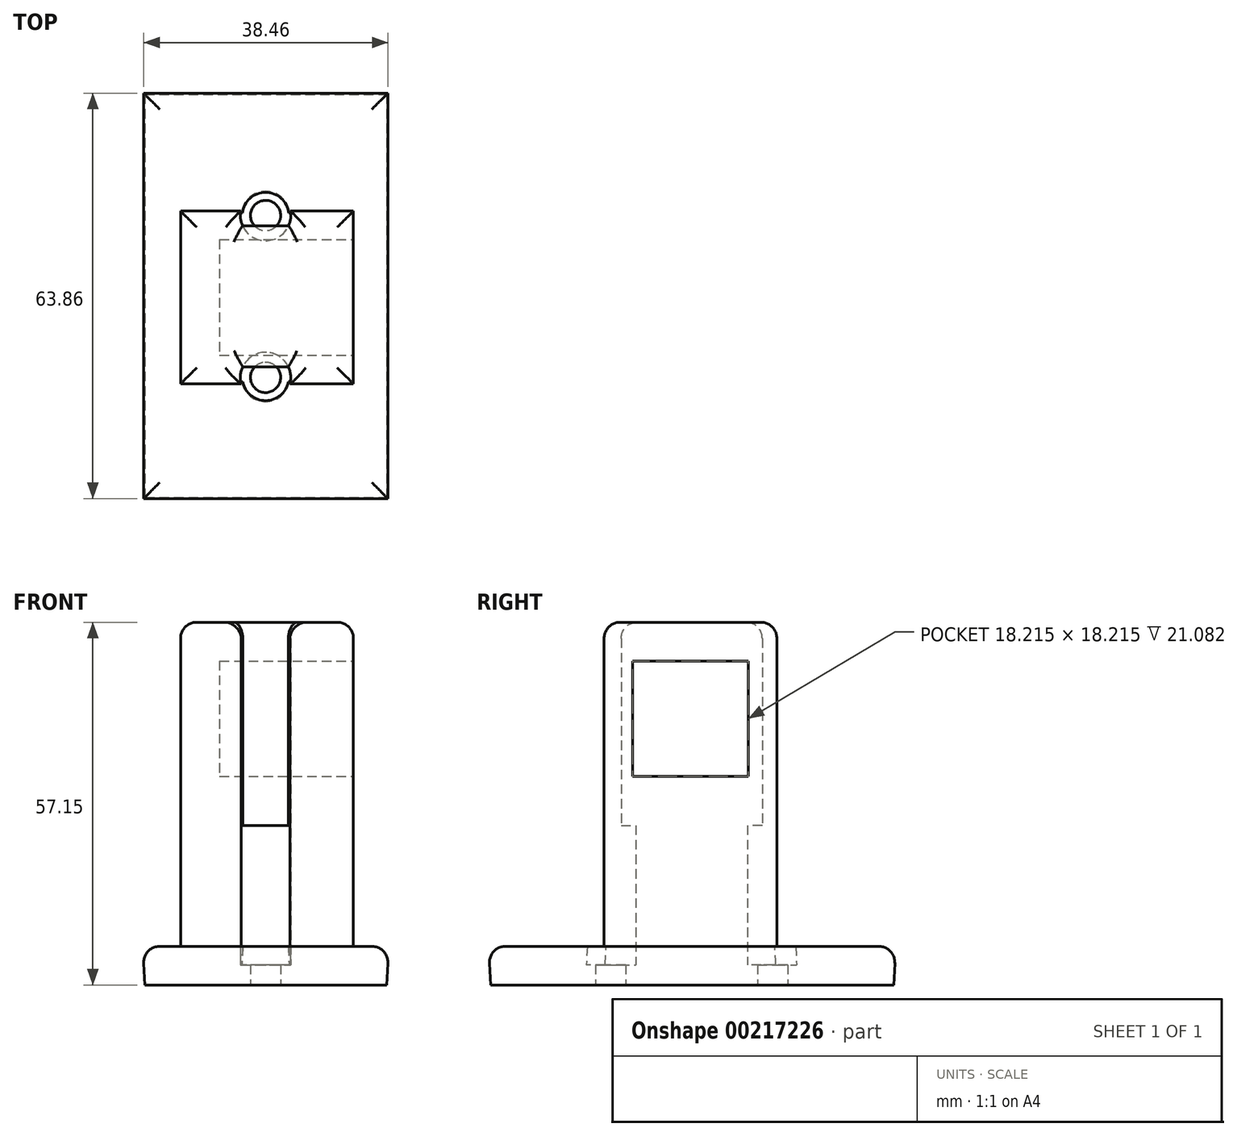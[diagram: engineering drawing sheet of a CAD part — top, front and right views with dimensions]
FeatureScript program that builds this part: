
annotation { "Feature Type Name" : "Feature", "Feature Type Description" : "" }
export const myFeature = defineFeature(function(context is Context, id is Id, definition is map)
    precondition{}
    {
        {
            var Q0;
            Q0=qCreatedBy(makeId("Top.planeOp"),FACE);
            var sketch = newSketch(context, id + "F0", { "sketchPlane" : qUnion([Q0])});
            skLineSegment(sketch, "E0.bottom", {"start": v(0, 0) * mm, "end": v(38.1, 0) * mm});
            skLineSegment(sketch, "E0.top", {"start": v(0, -63.5) * mm, "end": v(38.1, -63.5) * mm});
            skLineSegment(sketch, "E0.left", {"start": v(0, 0) * mm, "end": v(0, -63.5) * mm});
            skLineSegment(sketch, "E0.right", {"start": v(38.1, 0) * mm, "end": v(38.1, -63.5) * mm});
            skCircle(sketch, "E1", {"center": v(19.02, -19.09) * mm, "radius": 2.38 * mm});
            skCircle(sketch, "E2", {"center": v(19.02, -19.09) * mm, "radius": 3.97 * mm});
            skCircle(sketch, "E3", {"center": v(19.01, -44.6) * mm, "radius": 2.38 * mm});
            skCircle(sketch, "E4", {"center": v(19.01, -44.6) * mm, "radius": 3.97 * mm});
            skLineSegment(sketch, "E5", {"start": v(19.02, -19.09) * mm, "end": v(19.02, -44.49) * mm, "construction": true});
            skLineSegment(sketch, "E6", {"start": v(0, -31.75) * mm, "end": v(38.1, -31.75) * mm, "construction": true});
            skLineSegment(sketch, "E7", {"start": v(19.05, 0) * mm, "end": v(19.05, -63.5) * mm, "construction": true});
            skLineSegment(sketch, "E8.bottom", {"start": v(8.18, -20.7) * mm, "end": v(30.4, -20.7) * mm});
            skLineSegment(sketch, "E8.top", {"start": v(8.18, -42.93) * mm, "end": v(30.4, -42.93) * mm});
            skLineSegment(sketch, "E8.left", {"start": v(8.18, -20.7) * mm, "end": v(8.18, -42.93) * mm});
            skLineSegment(sketch, "E8.right", {"start": v(30.4, -20.7) * mm, "end": v(30.4, -42.93) * mm});
            skLineSegment(sketch, "E9.bottom", {"start": v(5.63, -18.4) * mm, "end": v(32.85, -18.4) * mm});
            skLineSegment(sketch, "E9.top", {"start": v(5.63, -45.62) * mm, "end": v(32.85, -45.62) * mm});
            skLineSegment(sketch, "E9.left", {"start": v(5.63, -18.4) * mm, "end": v(5.63, -45.62) * mm});
            skLineSegment(sketch, "E9.right", {"start": v(32.85, -18.4) * mm, "end": v(32.85, -45.62) * mm});
            skSolve(sketch);
        }
        {
            var Q0;
            {var subQ0=sQuery(id+"F0.wireOp",EDGE,"E8.bottom");var subQ1=sQuery(id+"F0.wireOp",EDGE,"E1");var subQ2=makeQuery(id+"F0.imprint","INTERSECT",VERTEX,{"disambiguationData":[OD(0.0)],"derivedFrom":[subQ1,subQ0]});Q0=makeQuery(id+"F0.imprint","IMPRINT",FACE,{"disambiguationData":[TD([[makeQuery(id+"F0.imprint","IMPRINT",EDGE,{"disambiguationData":[TD([[subQ2,-1.0]])],"derivedFrom":subQ1}),1.0]])]});}
            var Q1;
            {var subQ0=sQuery(id+"F0.wireOp",EDGE,"E8.bottom");var subQ1=sQuery(id+"F0.wireOp",EDGE,"E1");var subQ2=makeQuery(id+"F0.imprint","INTERSECT",VERTEX,{"disambiguationData":[OD(0.0)],"derivedFrom":[subQ1,subQ0]});Q1=makeQuery(id+"F0.imprint","IMPRINT",FACE,{"disambiguationData":[TD([[makeQuery(id+"F0.imprint","IMPRINT",EDGE,{"disambiguationData":[TD([[subQ2,-1.0]])],"derivedFrom":subQ1}),-1.0]])]});}
            var Q2;
            {var subQ0=sQuery(id+"F0.wireOp",EDGE,"E8.left");Q2=makeQuery(id+"F0.imprint","IMPRINT",FACE,{"disambiguationData":[TD([[makeQuery(id+"F0.imprint","IMPRINT",EDGE,{"derivedFrom":subQ0}),1.0]])]});}
            var Q3;
            {var subQ0=sQuery(id+"F0.wireOp",EDGE,"E8.top");var subQ1=sQuery(id+"F0.wireOp",EDGE,"E3");var subQ2=makeQuery(id+"F0.imprint","INTERSECT",VERTEX,{"disambiguationData":[OD(0.0)],"derivedFrom":[subQ1,subQ0]});Q3=makeQuery(id+"F0.imprint","IMPRINT",FACE,{"disambiguationData":[TD([[makeQuery(id+"F0.imprint","IMPRINT",EDGE,{"disambiguationData":[TD([[subQ2,1.0]])],"derivedFrom":subQ1}),-1.0]])]});}
            var Q4;
            {var subQ0=sQuery(id+"F0.wireOp",EDGE,"E8.top");var subQ1=sQuery(id+"F0.wireOp",EDGE,"E3");var subQ2=makeQuery(id+"F0.imprint","INTERSECT",VERTEX,{"disambiguationData":[OD(0.0)],"derivedFrom":[subQ1,subQ0]});Q4=makeQuery(id+"F0.imprint","IMPRINT",FACE,{"disambiguationData":[TD([[makeQuery(id+"F0.imprint","IMPRINT",EDGE,{"disambiguationData":[TD([[subQ2,1.0]])],"derivedFrom":subQ1}),1.0]])]});}
            var Q5;
            {var subQ0=sQuery(id+"F0.wireOp",EDGE,"E8.right");Q5=makeQuery(id+"F0.imprint","IMPRINT",FACE,{"disambiguationData":[TD([[makeQuery(id+"F0.imprint","IMPRINT",EDGE,{"derivedFrom":subQ0}),1.0]])]});}
            var Q6;
            {var subQ0=sQuery(id+"F0.wireOp",EDGE,"E8.left");Q6=makeQuery(id+"F0.imprint","IMPRINT",FACE,{"disambiguationData":[TD([[makeQuery(id+"F0.imprint","IMPRINT",EDGE,{"derivedFrom":subQ0}),-1.0]])]});}
            extrude(context, id + "F1", {"entities" : qUnion([Q0, Q1, Q2, Q3, Q4, Q5, Q6]), "depth" : 57.15 * mm});
        }
        {
            var Q0;
            {var subQ0=sQuery(id+"F0.wireOp",EDGE,"E8.left");Q0=makeQuery(id+"F0.imprint","IMPRINT",FACE,{"disambiguationData":[TD([[makeQuery(id+"F0.imprint","IMPRINT",EDGE,{"derivedFrom":subQ0}),-1.0]])]});}
            var Q1;
            {var subQ0=sQuery(id+"F0.wireOp",EDGE,"E8.right");Q1=makeQuery(id+"F0.imprint","IMPRINT",FACE,{"disambiguationData":[TD([[makeQuery(id+"F0.imprint","IMPRINT",EDGE,{"derivedFrom":subQ0}),1.0]])]});}
            extrude(context, id + "F2", {"entities" : qUnion([Q0, Q1]), "operationType" : NewBodyOperationType.ADD, "depth" : 15.2 * mm});
        }
        {
            var Q0;
            {var subQ0=sQuery(id+"F0.wireOp",EDGE,"E9.left");Q0=makeQuery(id+"F0.imprint","IMPRINT",FACE,{"disambiguationData":[TD([[makeQuery(id+"F0.imprint","IMPRINT",EDGE,{"derivedFrom":subQ0}),-1.0]])]});}
            extrude(context, id + "F3", {"entities" : qUnion([Q0]), "operationType" : NewBodyOperationType.ADD, "depth" : 6.1 * mm});
        }
        {
            var Q0;
            Q0=makeQuery(id+"F0.imprint","IMPRINT",FACE,{"disambiguationData":[TD([[makeQuery(id+"F0.imprint","IMPRINT",EDGE,{"derivedFrom":sQuery(id+"F0.wireOp",EDGE,"E0.bottom")}),-1.0]])]});
            extrude(context, id + "F4", {"entities" : qUnion([Q0]), "operationType" : NewBodyOperationType.ADD, "depth" : 6.1 * mm, "hasDraft" : true, "draftAngle" : 3 * degree});
        }
        {
            var Q0;
            {var subQ0=sQuery(id+"F0.wireOp",EDGE,"E8.bottom");var subQ1=sQuery(id+"F0.wireOp",EDGE,"E1");var subQ2=makeQuery(id+"F0.imprint","INTERSECT",VERTEX,{"disambiguationData":[OD(0.0)],"derivedFrom":[subQ1,subQ0]});Q0=makeQuery(id+"F0.imprint","IMPRINT",FACE,{"disambiguationData":[TD([[makeQuery(id+"F0.imprint","IMPRINT",EDGE,{"disambiguationData":[TD([[subQ2,-1.0]])],"derivedFrom":subQ1}),-1.0]])]});}
            var Q1;
            {var subQ0=sQuery(id+"F0.wireOp",EDGE,"E8.bottom");var subQ1=sQuery(id+"F0.wireOp",EDGE,"E1");var subQ2=makeQuery(id+"F0.imprint","INTERSECT",VERTEX,{"disambiguationData":[OD(0.0)],"derivedFrom":[subQ1,subQ0]});Q1=makeQuery(id+"F0.imprint","IMPRINT",FACE,{"disambiguationData":[TD([[makeQuery(id+"F0.imprint","IMPRINT",EDGE,{"disambiguationData":[TD([[subQ2,-1.0]])],"derivedFrom":subQ1}),1.0]])]});}
            var Q2;
            {var subQ0=sQuery(id+"F0.wireOp",EDGE,"E8.top");var subQ1=sQuery(id+"F0.wireOp",EDGE,"E3");var subQ2=makeQuery(id+"F0.imprint","INTERSECT",VERTEX,{"disambiguationData":[OD(0.0)],"derivedFrom":[subQ1,subQ0]});Q2=makeQuery(id+"F0.imprint","IMPRINT",FACE,{"disambiguationData":[TD([[makeQuery(id+"F0.imprint","IMPRINT",EDGE,{"disambiguationData":[TD([[subQ2,1.0]])],"derivedFrom":subQ1}),1.0]])]});}
            var Q3;
            {var subQ0=sQuery(id+"F0.wireOp",EDGE,"E8.top");var subQ1=sQuery(id+"F0.wireOp",EDGE,"E3");var subQ2=makeQuery(id+"F0.imprint","INTERSECT",VERTEX,{"disambiguationData":[OD(0.0)],"derivedFrom":[subQ1,subQ0]});Q3=makeQuery(id+"F0.imprint","IMPRINT",FACE,{"disambiguationData":[TD([[makeQuery(id+"F0.imprint","IMPRINT",EDGE,{"disambiguationData":[TD([[subQ2,1.0]])],"derivedFrom":subQ1}),-1.0]])]});}
            extrude(context, id + "F5", {"entities" : qUnion([Q0, Q1, Q2, Q3]), "operationType" : NewBodyOperationType.REMOVE, "depth" : 25.15 * mm});
        }
        {
            var Q0;
            Q0=makeQuery(id+"F4.opExtrude","CAP_EDGE",EDGE,{"disambiguationData":[OSD([sQuery(id+"F0.wireOp",EDGE,"E0.right")])],"isStart":false});
            var Q1;
            Q1=makeQuery(id+"F4.opExtrude","CAP_EDGE",EDGE,{"disambiguationData":[OSD([sQuery(id+"F0.wireOp",EDGE,"E0.bottom")])],"isStart":false});
            var Q2;
            Q2=makeQuery(id+"F4.opExtrude","CAP_EDGE",EDGE,{"disambiguationData":[OSD([sQuery(id+"F0.wireOp",EDGE,"E0.top")])],"isStart":false});
            var Q3;
            Q3=makeQuery(id+"F4.opExtrude","CAP_EDGE",EDGE,{"disambiguationData":[OSD([sQuery(id+"F0.wireOp",EDGE,"E0.left")])],"isStart":false});
            fillet(context, id + "F6", {"entities" : qUnion([Q0, Q1, Q2, Q3]), "radius" : 2.54 * mm, "tangentPropagation" : true, "allowEdgeOverflow" : false});
        }
        {
            var Q0;
            Q0=makeQuery(id+"F1.opExtrude","CAP_FACE",FACE,{"disambiguationData":[OSD([sQuery(id+"F0.wireOp",EDGE,"E8.bottom"),sQuery(id+"F0.wireOp",EDGE,"E8.top"),sQuery(id+"F0.wireOp",EDGE,"E8.left"),sQuery(id+"F0.wireOp",EDGE,"E8.right")])],"isStart":false});
            fillet(context, id + "F7", {"entities" : qUnion([Q0]), "radius" : 2.54 * mm, "tangentPropagation" : true, "allowEdgeOverflow" : false});
        }
        {
            var Q0;
            {var subQ0=sQuery(id+"F0.wireOp",EDGE,"E9.bottom");var subQ1=sQuery(id+"F0.wireOp",EDGE,"E1");var subQ2=makeQuery(id+"F0.imprint","INTERSECT",VERTEX,{"disambiguationData":[OD(0.0)],"derivedFrom":[subQ1,subQ0]});Q0=makeQuery(id+"F0.imprint","IMPRINT",FACE,{"disambiguationData":[TD([[makeQuery(id+"F0.imprint","IMPRINT",EDGE,{"disambiguationData":[TD([[subQ2,1.0]])],"derivedFrom":subQ1}),-1.0]])]});}
            var Q1;
            {var subQ0=sQuery(id+"F0.wireOp",EDGE,"E9.bottom");var subQ1=sQuery(id+"F0.wireOp",EDGE,"E1");var subQ2=makeQuery(id+"F0.imprint","INTERSECT",VERTEX,{"disambiguationData":[OD(0.0)],"derivedFrom":[subQ1,subQ0]});Q1=makeQuery(id+"F0.imprint","IMPRINT",FACE,{"disambiguationData":[TD([[makeQuery(id+"F0.imprint","IMPRINT",EDGE,{"disambiguationData":[TD([[subQ2,-1.0]])],"derivedFrom":subQ1}),-1.0]])]});}
            var Q2;
            {var subQ0=sQuery(id+"F0.wireOp",EDGE,"E8.bottom");var subQ1=sQuery(id+"F0.wireOp",EDGE,"E1");var subQ2=makeQuery(id+"F0.imprint","INTERSECT",VERTEX,{"disambiguationData":[OD(0.0)],"derivedFrom":[subQ1,subQ0]});Q2=makeQuery(id+"F0.imprint","IMPRINT",FACE,{"disambiguationData":[TD([[makeQuery(id+"F0.imprint","IMPRINT",EDGE,{"disambiguationData":[TD([[subQ2,-1.0]])],"derivedFrom":subQ1}),-1.0]])]});}
            var Q3;
            {var subQ0=sQuery(id+"F0.wireOp",EDGE,"E9.bottom");var subQ1=sQuery(id+"F0.wireOp",EDGE,"E1");var subQ2=makeQuery(id+"F0.imprint","INTERSECT",VERTEX,{"disambiguationData":[OD(1.0)],"derivedFrom":[subQ1,subQ0]});Q3=makeQuery(id+"F0.imprint","IMPRINT",FACE,{"disambiguationData":[TD([[makeQuery(id+"F0.imprint","IMPRINT",EDGE,{"disambiguationData":[TD([[subQ2,1.0]])],"derivedFrom":subQ1}),-1.0]])]});}
            var Q4;
            {var subQ0=sQuery(id+"F0.wireOp",EDGE,"E9.top");var subQ1=sQuery(id+"F0.wireOp",EDGE,"E3");var subQ2=makeQuery(id+"F0.imprint","INTERSECT",VERTEX,{"disambiguationData":[OD(0.0)],"derivedFrom":[subQ1,subQ0]});Q4=makeQuery(id+"F0.imprint","IMPRINT",FACE,{"disambiguationData":[TD([[makeQuery(id+"F0.imprint","IMPRINT",EDGE,{"disambiguationData":[TD([[subQ2,-1.0]])],"derivedFrom":subQ1}),-1.0]])]});}
            var Q5;
            {var subQ0=sQuery(id+"F0.wireOp",EDGE,"E8.top");var subQ1=sQuery(id+"F0.wireOp",EDGE,"E3");var subQ2=makeQuery(id+"F0.imprint","INTERSECT",VERTEX,{"disambiguationData":[OD(1.0)],"derivedFrom":[subQ1,subQ0]});Q5=makeQuery(id+"F0.imprint","IMPRINT",FACE,{"disambiguationData":[TD([[makeQuery(id+"F0.imprint","IMPRINT",EDGE,{"disambiguationData":[TD([[subQ2,1.0]])],"derivedFrom":subQ1}),-1.0]])]});}
            var Q6;
            {var subQ0=sQuery(id+"F0.wireOp",EDGE,"E8.top");var subQ1=sQuery(id+"F0.wireOp",EDGE,"E3");var subQ2=makeQuery(id+"F0.imprint","INTERSECT",VERTEX,{"disambiguationData":[OD(0.0)],"derivedFrom":[subQ1,subQ0]});Q6=makeQuery(id+"F0.imprint","IMPRINT",FACE,{"disambiguationData":[TD([[makeQuery(id+"F0.imprint","IMPRINT",EDGE,{"disambiguationData":[TD([[subQ2,1.0]])],"derivedFrom":subQ1}),-1.0]])]});}
            var Q7;
            {var subQ0=sQuery(id+"F0.wireOp",EDGE,"E8.top");var subQ1=sQuery(id+"F0.wireOp",EDGE,"E3");var subQ2=makeQuery(id+"F0.imprint","INTERSECT",VERTEX,{"disambiguationData":[OD(0.0)],"derivedFrom":[subQ1,subQ0]});Q7=makeQuery(id+"F0.imprint","IMPRINT",FACE,{"disambiguationData":[TD([[makeQuery(id+"F0.imprint","IMPRINT",EDGE,{"disambiguationData":[TD([[subQ2,-1.0]])],"derivedFrom":subQ1}),-1.0]])]});}
            extrude(context, id + "F8", {"entities" : qUnion([Q0, Q1, Q2, Q3, Q4, Q5, Q6, Q7]), "operationType" : NewBodyOperationType.ADD, "depth" : 3.17 * mm});
        }
        {
            var Q0;
            Q0=makeQuery(id+"F1.opExtrude","SWEPT_FACE",FACE,{"disambiguationData":[OSD([sQuery(id+"F0.wireOp",EDGE,"E9.right")])]});
            var sketch = newSketch(context, id + "F9", { "sketchPlane" : qUnion([Q0])});
            skLineSegment(sketch, "E10.bottom", {"start": v(-22.9, 51.06) * mm, "end": v(-41.12, 51.06) * mm});
            skLineSegment(sketch, "E10.top", {"start": v(-22.9, 32.84) * mm, "end": v(-41.12, 32.84) * mm});
            skLineSegment(sketch, "E10.left", {"start": v(-22.9, 51.06) * mm, "end": v(-22.9, 32.84) * mm});
            skLineSegment(sketch, "E10.right", {"start": v(-41.12, 51.06) * mm, "end": v(-41.12, 32.84) * mm});
            skSolve(sketch);
        }
        {
            var Q0;
            Q0=makeQuery(id+"F9.imprint","IMPRINT",FACE,{"disambiguationData":[TD([[makeQuery(id+"F9.imprint","IMPRINT",EDGE,{"derivedFrom":sQuery(id+"F9.wireOp",EDGE,"E10.bottom")}),1.0]])]});
            extrude(context, id + "F10", {"entities" : qUnion([Q0]), "operationType" : NewBodyOperationType.REMOVE, "oppositeDirection" : true, "depth" : 21.08 * mm});
        }
    });
